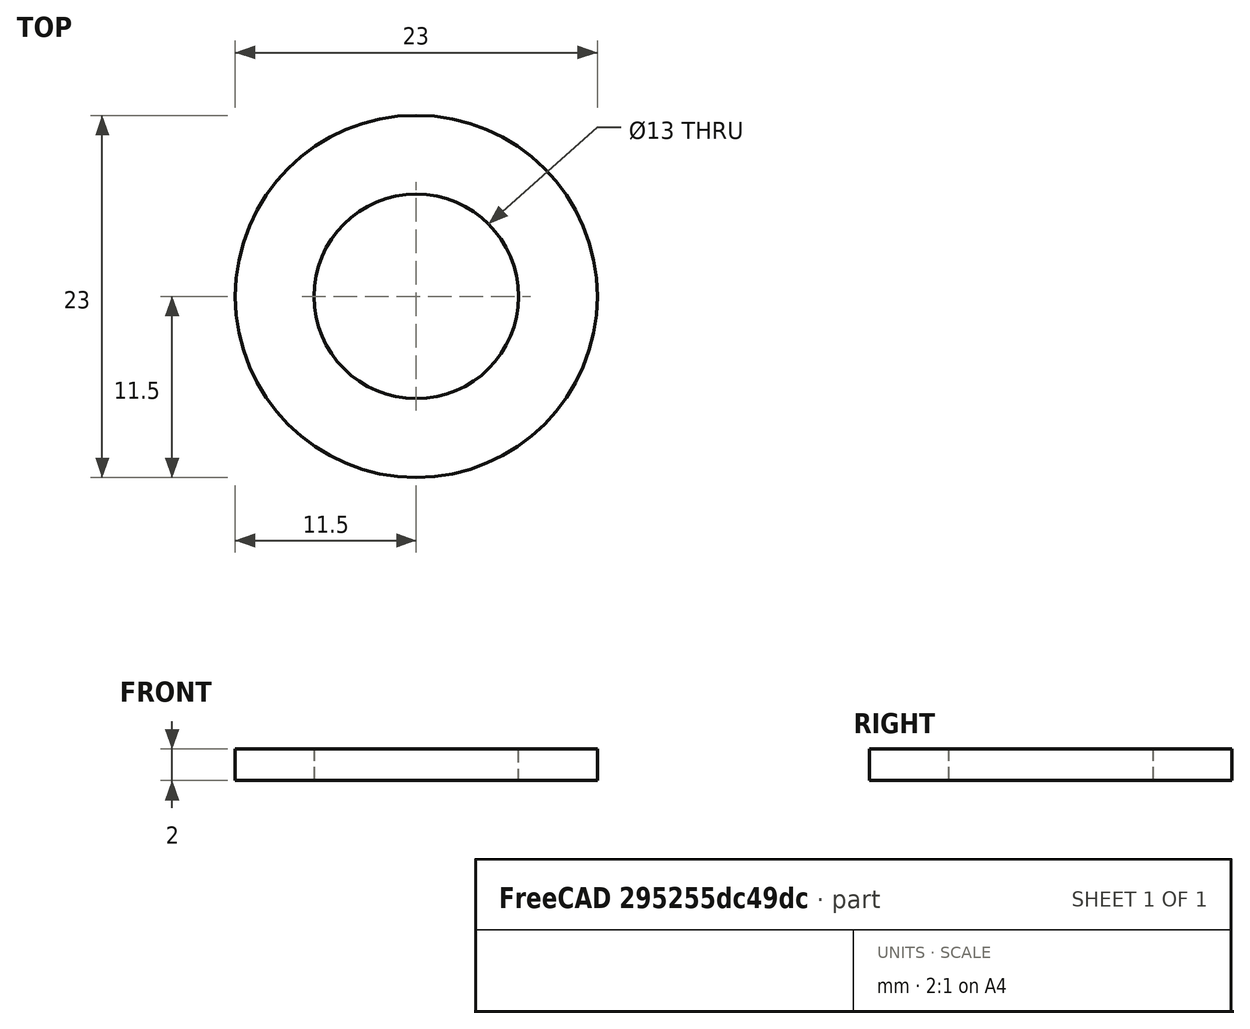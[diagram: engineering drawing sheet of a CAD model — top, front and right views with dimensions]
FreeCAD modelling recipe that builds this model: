
FCSTD DOCUMENT  (FreeCAD 0.19R24276 (Git))
Label: Ring_d13_d23_h2
License: All rights reserved
LicenseURL: http://en.wikipedia.org/wiki/All_rights_reserved
objects: Sketcher::SketchObject×1, PartDesign::Pad×1, PartDesign::Body×1
note: 4 computed .brp shape members not serialized (recipe doc carries the construction recipe); baked Part::Feature solids carry a one-line shape summary decoded from their .brp

FEATURE [Sketcher::SketchObject] Sketch
  FullyConstrained = true
  MapMode = 5
  Support = -> [XY_Plane]
  sketch-geometry (2):
    g0: Circle CenterX=0 CenterY=0 CenterZ=0 NormalX=0 NormalY=0 NormalZ=1 AngleXU=0 Radius=6.5
    g1: Circle CenterX=0 CenterY=0 CenterZ=0 NormalX=0 NormalY=0 NormalZ=1 AngleXU=0 Radius=11.5
  constraints (4):
    c: Coincident(g0,g-1)
    c: Coincident(g1,g0)
    c: Diameter(g0) = 13
    c: Diameter(g1) = 23
FEATURE [PartDesign::Pad] Pad
  Direction = (1,1,1)
  Length = 2
  Length2 = 100
  Profile = -> Sketch
  Type = 0
FEATURE [PartDesign::Body] Body
  Group = -> [Sketch,Pad]
  Origin = -> Origin
  Tip = -> Pad
